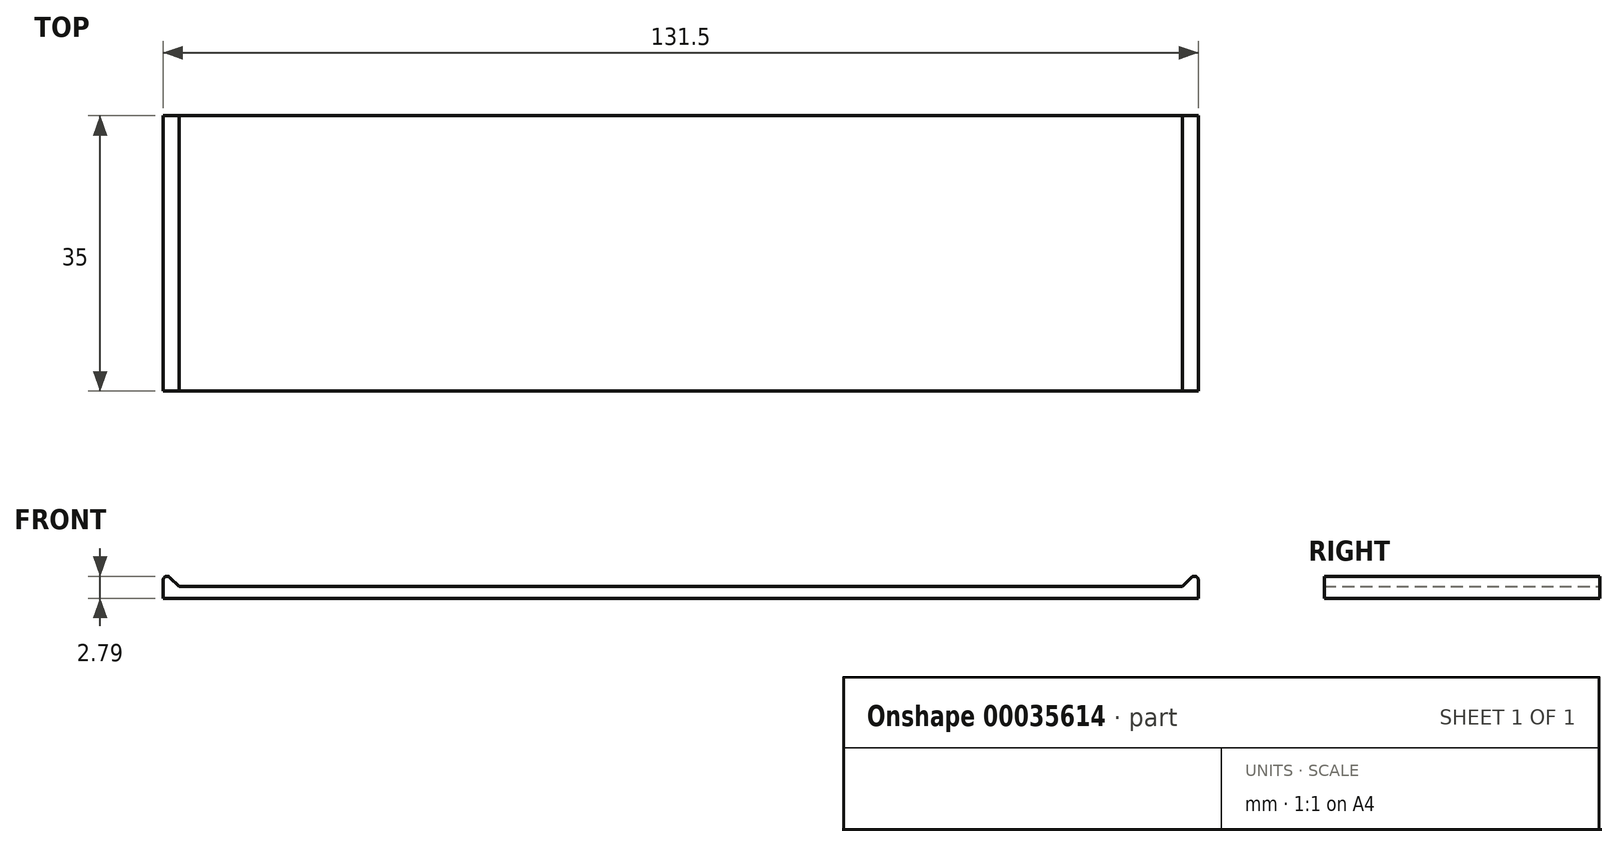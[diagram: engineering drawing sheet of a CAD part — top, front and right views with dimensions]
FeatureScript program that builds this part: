
annotation { "Feature Type Name" : "Feature", "Feature Type Description" : "" }
export const myFeature = defineFeature(function(context is Context, id is Id, definition is map)
    precondition{}
    {
        {
            var Q0;
            Q0=qCreatedBy(makeId("Front.planeOp"),FACE);
            var sketch = newSketch(context, id + "F0", { "sketchPlane" : qUnion([Q0])});
            skLineSegment(sketch, "E0.bottom", {"start": v(-65.75, 0) * mm, "end": v(65.75, 0) * mm});
            skLineSegment(sketch, "E0.top", {"start": v(-65.75, 1.5) * mm, "end": v(65.75, 1.5) * mm});
            skLineSegment(sketch, "E0.left", {"start": v(-65.75, 0) * mm, "end": v(-65.75, 1.5) * mm});
            skLineSegment(sketch, "E0.right", {"start": v(65.75, 0) * mm, "end": v(65.75, 1.5) * mm});
            skLineSegment(sketch, "E1", {"start": v(-65.75, 1.5) * mm, "end": v(-65.75, 3.5) * mm});
            skLineSegment(sketch, "E2", {"start": v(-65.75, 3.5) * mm, "end": v(-63.75, 1.5) * mm});
            skLineSegment(sketch, "E3", {"start": v(65.75, 1.5) * mm, "end": v(65.75, 3.5) * mm});
            skLineSegment(sketch, "E4", {"start": v(65.75, 3.5) * mm, "end": v(63.75, 1.5) * mm});
            skSolve(sketch);
        }
        {
            var Q0;
            Q0=qSketchRegion(id+"F0",true);
            extrude(context, id + "F1", {"entities" : qUnion([Q0]), "depth" : 35 * mm, "symmetric" : true});
        }
        {
            var Q0;
            Q0=makeQuery(id+"F1.opExtrude","SWEPT_EDGE",EDGE,{"disambiguationData":[OSD([sQuery(id+"F0.wireOp",EDGE,"E1"),sQuery(id+"F0.wireOp",EDGE,"E2")])]});
            var Q1;
            Q1=makeQuery(id+"F1.opExtrude","SWEPT_EDGE",EDGE,{"disambiguationData":[OSD([sQuery(id+"F0.wireOp",EDGE,"E3"),sQuery(id+"F0.wireOp",EDGE,"E4")])]});
            fillet(context, id + "F2", {"entities" : qUnion([Q0, Q1]), "radius" : .5 * mm, "tangentPropagation" : true, "allowEdgeOverflow" : false});
        }
    });
